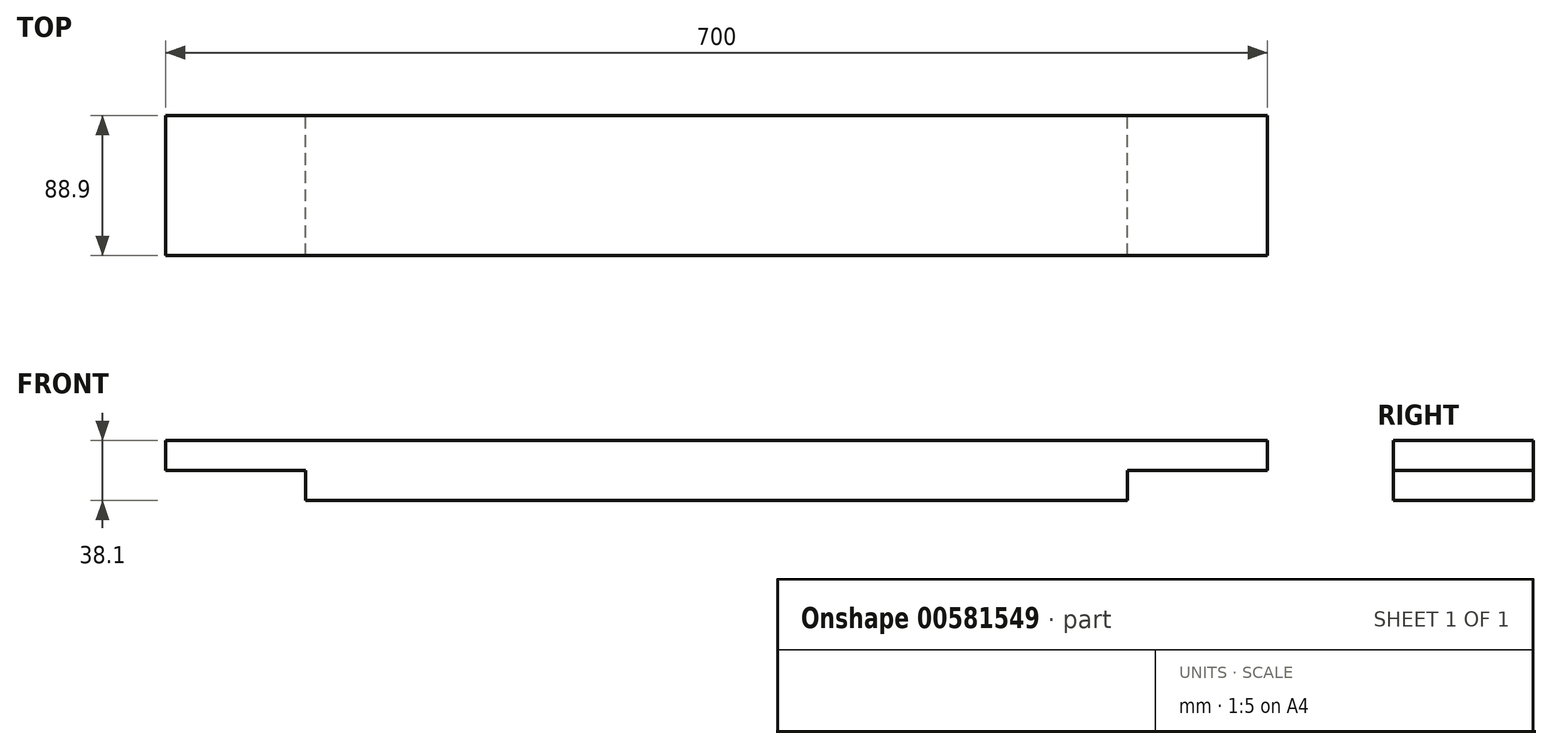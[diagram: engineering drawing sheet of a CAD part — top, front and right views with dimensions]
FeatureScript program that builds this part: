
annotation { "Feature Type Name" : "Feature", "Feature Type Description" : "" }
export const myFeature = defineFeature(function(context is Context, id is Id, definition is map)
    precondition{}
    {
        {
            var Q0;
            Q0=qCreatedBy(makeId("Top.planeOp"),FACE);
            var sketch = newSketch(context, id + "F0", { "sketchPlane" : qUnion([Q0])});
            skLineSegment(sketch, "E0.bottom", {"start": v(350, 44.45) * mm, "end": v(-350, 44.45) * mm});
            skLineSegment(sketch, "E0.top", {"start": v(350, -44.45) * mm, "end": v(-350, -44.45) * mm});
            skLineSegment(sketch, "E0.left", {"start": v(350, 44.45) * mm, "end": v(350, -44.45) * mm});
            skLineSegment(sketch, "E0.right", {"start": v(-350, 44.45) * mm, "end": v(-350, -44.45) * mm});
            skPoint(sketch, "E0.middle", {"position": v(0, 0) * mm});
            skSolve(sketch);
        }
        {
            var Q0;
            Q0 = qSketchRegion(id + "F0", true);
            extrude(context, id + "F1", {"entities" : qUnion([Q0]), "depth" : 38.1 * mm, "offsetDistance" : 25.4 * mm});
        }
        {
            var Q0;
            Q0=makeQuery(id+"F1.opExtrude","SWEPT_FACE",FACE,{"disambiguationData":[OSD([sQuery(id+"F0.wireOp",EDGE,"E0.bottom")])]});
            var sketch = newSketch(context, id + "F2", { "sketchPlane" : qUnion([Q0])});
            skLineSegment(sketch, "E1.bottom", {"start": v(350, 0) * mm, "end": v(261.1, 0) * mm});
            skLineSegment(sketch, "E1.top", {"start": v(350, 19.05) * mm, "end": v(261.1, 19.05) * mm});
            skLineSegment(sketch, "E1.left", {"start": v(350, 0) * mm, "end": v(350, 19.05) * mm});
            skLineSegment(sketch, "E1.right", {"start": v(261.1, 0) * mm, "end": v(261.1, 19.05) * mm});
            skLineSegment(sketch, "E2.MirrorCS", {"start": v(-350, 19.05) * mm, "end": v(-261.1, 19.05) * mm});
            skLineSegment(sketch, "E3.MirrorCS", {"start": v(-261.1, 0) * mm, "end": v(-261.1, 19.05) * mm});
            skLineSegment(sketch, "E4.MirrorCS", {"start": v(-350, 0) * mm, "end": v(-261.1, 0) * mm});
            skLineSegment(sketch, "E5.MirrorCS", {"start": v(-350, 0) * mm, "end": v(-350, 19.05) * mm});
            skSolve(sketch);
        }
        {
            var Q0;
            Q0=makeQuery(id+"F2.imprint","IMPRINT",FACE,{"disambiguationData":[TD([[makeQuery(id+"F2.imprint","IMPRINT",EDGE,{"derivedFrom":sQuery(id+"F2.wireOp",EDGE,"E1.bottom")}),1.0]])]});
            var Q1;
            Q1=makeQuery(id+"F2.imprint","IMPRINT",FACE,{"disambiguationData":[TD([[makeQuery(id+"F2.imprint","IMPRINT",EDGE,{"derivedFrom":sQuery(id+"F2.wireOp",EDGE,"E2.MirrorCS")}),-1.0]])]});
            var Q2;
            Q2=makeQuery(id+"F1.opExtrude","SWEPT_FACE",FACE,{"disambiguationData":[OSD([sQuery(id+"F0.wireOp",EDGE,"E0.top")])]});
            extrude(context, id + "F3", {"entities" : qUnion([Q0, Q1]), "operationType" : NewBodyOperationType.REMOVE, "endBound" : BoundingType.UP_TO_SURFACE, "oppositeDirection" : true, "depth" : 30.73 * mm, "endBoundEntityFace" : qUnion([Q2]), "offsetDistance" : 25.4 * mm});
        }
    });
